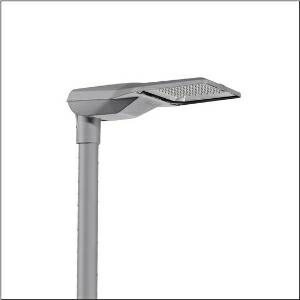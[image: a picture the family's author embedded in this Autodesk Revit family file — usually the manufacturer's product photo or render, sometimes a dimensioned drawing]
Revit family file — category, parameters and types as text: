
# Revit family: streetlight_sl_21_iq_midi___p0_5a_5xe3v31g08mb_4daf
name_source: partatom
category: Lighting Fixtures
units: mm (PartAtom-declared; Revit-internal decimal feet)

## family parameters
Cut with Voids When Loaded = No
Host = Face
Light Source = No
Part Type = Normal
Room Calculation Point = No
Round Connector Dimension = Use Diameter
Shared = No

## types (1)
- --- (1 x LED, 19170 lm, 146.7 W, 3000K)
    Apparent Load = 147 VA
    CIE Flux Codes = 37 73 96 100 100
    Color Rendering = 70
    Color Temperature = 3000K
    Default Elevation = 1800 mm
    Description = Streetlight SL 21 iQ midi, mast luminaire, primary light control with lens, of PMMA, primary optical cover: cover, of toughened safety glass, transparent, light distribution: P0.5a, light emission: direct distribution, primary light characteristic: asymmetric, installation type: post-top, side-entry, LED, High Power LED, rated luminous flux: 19.170lm, luminous efficacy: 131lm/W, light colour: 730, colour temperature: 3000K, control gear: iQ Street-Remote, control: pre-setting: linear dimming characteristic, Street-Remote, Auto-Match, Temp-Guard, Lumen-Switch, Night-Set, Smart-Wire, Light-Fading, Desk-Remote (wireless, voltage-free reading and setting of iQ features in the workshop via application-optimized NFC function/RFID function), optimised constant luminous flux control (CLO 2.0), mains connection: 230..240V, AC, 50/60Hz, start of lifetime: 147W, end of service life: 161W, reduction: 62W, luminaire housing, of diecast aluminium, powder-coated, Siteco® metallic grey (DB 702S), corrosivity category C5 mid according to DIN EN ISO 12944, please order mast flange separately, inclination adjustable: 0°, 5°, 10°, 15°, sealing non-destructively replaceable, multi-level sealing system, length: 644mm, width: 335mm, height: 110mm, mast flange for spigot size: 42mm (side-entry): 5XC10008XM4, 60/48mm (side-entry/post-top): 5XC10108XM2, 76/60mm (side-entry/post-top): 5XC10108XM1, mounting height: 4..8m, protection rating (complete): IP66, insulation class (complete): insulation class II (safety insulation), certification: CE, ENEC, ENEC+, VDE, impact resistance: IK10, permissible operating ambient temperature for outdoor applications: -40..+50°C, standard-compliant lighting for roads and squares, packaging unit: 1 piece

Light Distribution: P0.5a
    Height = 111 mm
    Lamp = 1 x LED
    Lamp Light Flux = 19170 lm
    Lamp Power = 146.7 W
    Lamp count = 1
    Length = 644 mm
    Luminous efficacy = 131 lm/W
    Manufacturer = Siteco
    ModVariant = No
    Model = 5XE3V31G08MB
    Number of Poles = 1
    OnlyDefault = Yes
    Power Factor = 1
    Product Name = Streetlight SL 21 iQ midi | P0.5a
    Product group = mast luminaire | pylon top
    ProductGroupID = 6100
    Protection Class = Protection class II
    Protection Degree = IP 66
    RLX_Detail_Level = 1
    RLX_Emergency_Light_Flux = 0 lm
    RLX_Emergency_Type = 0
    RLX_Emergency_Type_DB = No
    RlxData = <blob elided: 89741 chars, md5=64578fe9>
    Socket = socket
    Standby Power = 0 W
    System Light Flux = 19169 lm
    System Power = 147 W
    Type Comments = factory setting: luminous flux: 100 % | dim-lin: 254 | 753 mA
    Type Image = l_1004298.jpg
    URL = http://relux.com
    VarID = @adj_091139
    Voltage = 0 V
    Weight = 0.00 kg
    Width = 336 mm

## geometry (parser evidence)
native form markers: Blend x4, Sweep x12
no freeform markers — native parametric forms only
